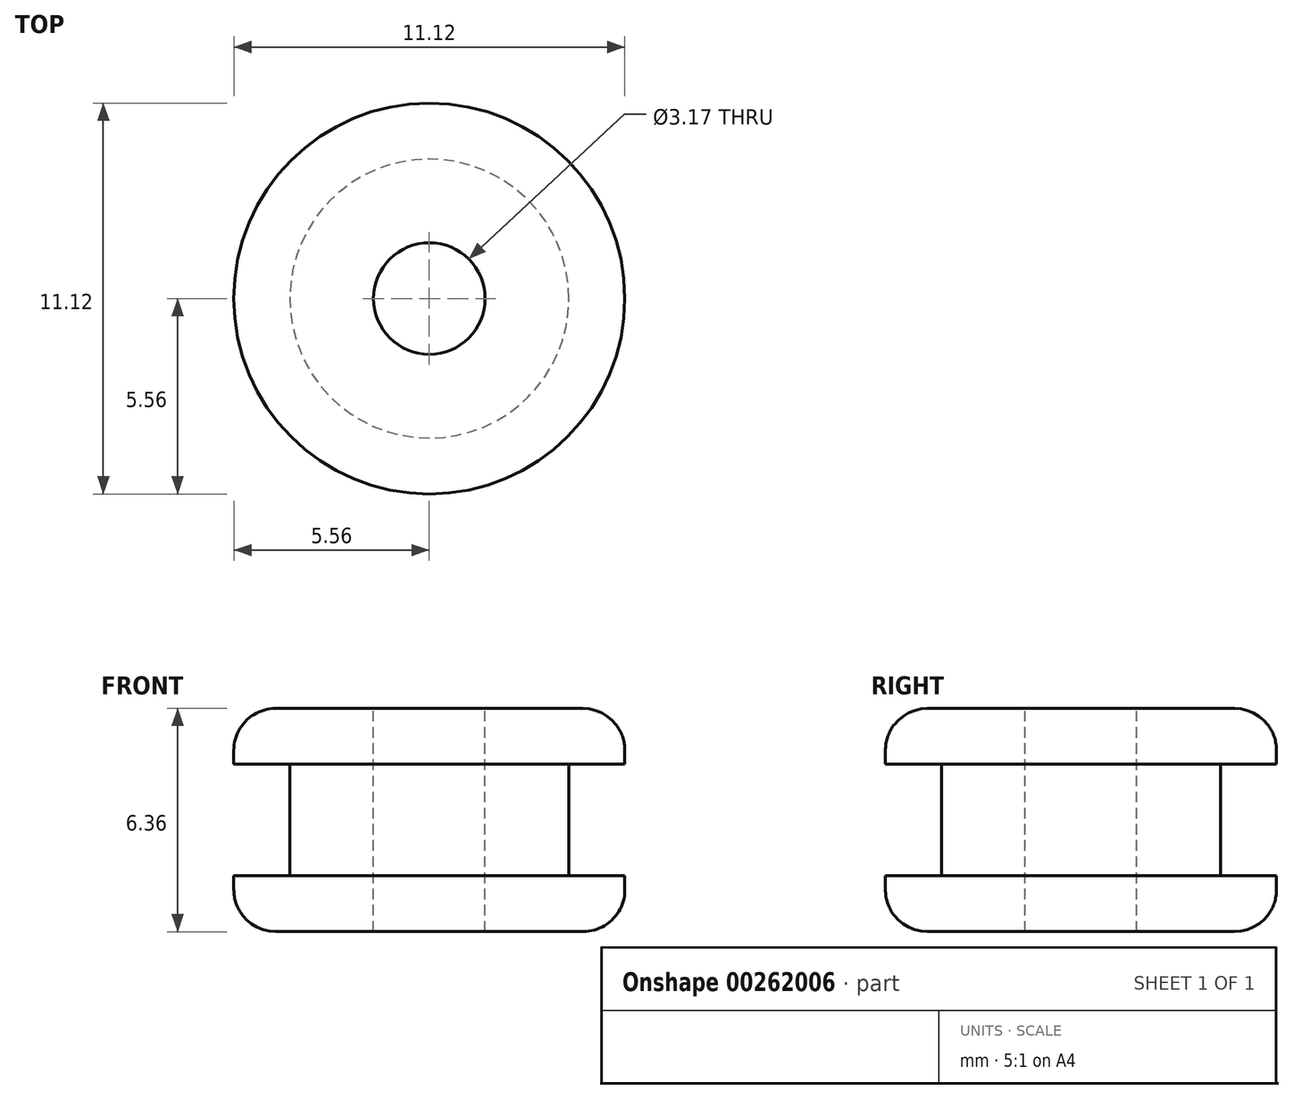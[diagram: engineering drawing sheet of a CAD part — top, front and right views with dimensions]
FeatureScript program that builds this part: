
annotation { "Feature Type Name" : "Feature", "Feature Type Description" : "" }
export const myFeature = defineFeature(function(context is Context, id is Id, definition is map)
    precondition{}
    {
        {
            assignVariable(context, id + "F0", {"name" : "A_ID", "anyValue" : 3.17});
        }
        {
            assignVariable(context, id + "F1", {"name" : "A_r", "anyValue" : getVariable(context, 'A_ID') / 2 * mm});
        }
        {
            var Q0;
            Q0=qCreatedBy(makeId("Front.planeOp"),FACE);
            var sketch = newSketch(context, id + "F2", { "sketchPlane" : qUnion([Q0])});
            skLineSegment(sketch, "E0", {"start": v(0, 12.22) * mm, "end": v(0, -12.17) * mm, "construction": true});
            skLineSegment(sketch, "E1", {"start": v(-1.59, 3.18) * mm, "end": v(-1.59, -3.18) * mm});
            skLineSegment(sketch, "E2", {"start": v(-1.59, -3.18) * mm, "end": v(-5.56, -3.18) * mm});
            skLineSegment(sketch, "E3", {"start": v(-5.56, -3.17) * mm, "end": v(-5.56, -1.59) * mm});
            skLineSegment(sketch, "E4", {"start": v(-5.56, -1.59) * mm, "end": v(-3.97, -1.59) * mm});
            skLineSegment(sketch, "E5", {"start": v(-3.97, -1.59) * mm, "end": v(-3.97, 1.59) * mm});
            skLineSegment(sketch, "E6", {"start": v(-3.97, 1.59) * mm, "end": v(-5.56, 1.59) * mm});
            skLineSegment(sketch, "E7", {"start": v(-5.56, 1.59) * mm, "end": v(-5.56, 3.17) * mm});
            skLineSegment(sketch, "E8", {"start": v(-5.56, 3.17) * mm, "end": v(-1.59, 3.17) * mm});
            skPoint(sketch, "E9", {"position": v(-1.59, 0) * mm});
            skPoint(sketch, "E9.positionSnap0", {"position": v(-1.59, 0) * mm});
            skPoint(sketch, "E10", {"position": v(-3.97, 0) * mm});
            skSolve(sketch);
        }
        {
            var Q0;
            Q0=makeQuery(id+"F2.imprint","IMPRINT",FACE,{"disambiguationData":[TD([[makeQuery(id+"F2.imprint","IMPRINT",EDGE,{"derivedFrom":sQuery(id+"F2.wireOp",EDGE,"E1")}),-1.0]])]});
            var Q1;
            Q1=sQuery(id+"F2.wireOp",EDGE,"E0");
            revolve(context, id + "F3", {"entities" : qUnion([Q0]), "axis" : qUnion([Q1]), "revolveType" : RevolveType.FULL});
        }
        {
            var Q0;
            Q0=makeQuery(id+"F3.opRevolve","SWEPT_EDGE",EDGE,{"disambiguationData":[OSD([sQuery(id+"F2.wireOp",EDGE,"E7"),sQuery(id+"F2.wireOp",EDGE,"E8")])]});
            fillet(context, id + "F4", {"entities" : qUnion([Q0]), "radius" : getVariable(context, 'A_r') * .75, "tangentPropagation" : true, "allowEdgeOverflow" : false});
        }
        {
            var Q0;
            Q0=makeQuery(id+"F3.opRevolve","SWEPT_EDGE",EDGE,{"disambiguationData":[OSD([sQuery(id+"F2.wireOp",EDGE,"E2"),sQuery(id+"F2.wireOp",EDGE,"E3")])]});
            fillet(context, id + "F5", {"entities" : qUnion([Q0]), "radius" : getVariable(context, 'A_r') * .75, "tangentPropagation" : true, "allowEdgeOverflow" : false});
        }
    });
